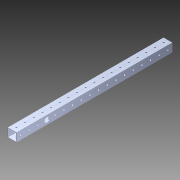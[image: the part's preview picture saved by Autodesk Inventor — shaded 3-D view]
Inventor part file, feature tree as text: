
AUTODESK INVENTOR PART (.ipt)
format: ipt  version: 2014 (Build 180170000, 170)  size: 1,283,072 bytes
history: native  units: in
note: dims shown in document units (in); Inventor stores cm internally (conversion verified against a paired STEP export)
features: sketch x3, extrude x2, pattern_circular x1, other x1, plane x1, imported_body x1
ambient origin geometry x8: Origin, YZ Plane, XZ Plane, XY Plane, X Axis, Y Axis, Z Axis, Center Point
bodies: Body1 (feature_tree)
feature tree (9):
  pattern_circular  "CirPattern2"
  other  "217-3426-STEP1"
  plane  "Work Plane1"
  extrude  "Extrusion1"  Depth=3937.0079in TaperAngle=0.0deg
  sketch  "Sketch3"  dims[d3=0.5in d5=2.0in d6=0.0in]
  extrude  "Extrusion2"  Depth=0.5in TaperAngle=0.0deg
  imported_body  "Base1"
  sketch  "Sketch1"  dims[d0=-18.0in d1=3937.0079in d2=0.0in]
  sketch  "Sketch4"
